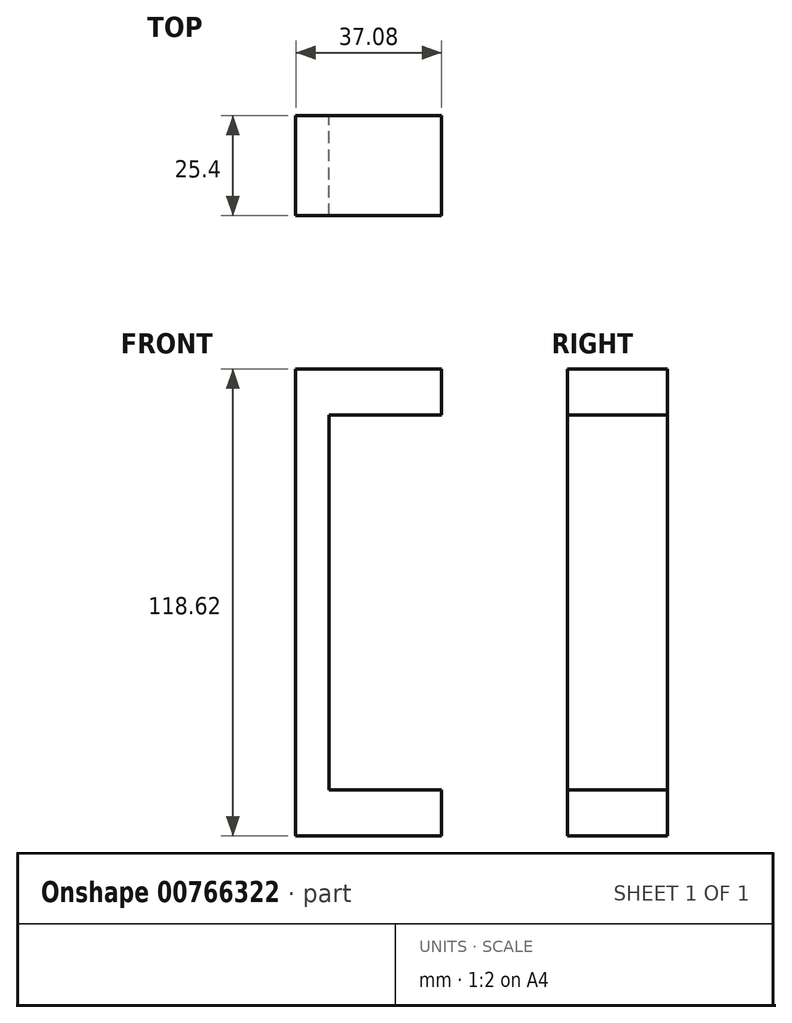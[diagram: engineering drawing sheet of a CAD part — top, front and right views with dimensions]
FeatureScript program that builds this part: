
annotation { "Feature Type Name" : "Feature", "Feature Type Description" : "" }
export const myFeature = defineFeature(function(context is Context, id is Id, definition is map)
    precondition{}
    {
        {
            var Q0;
            Q0=qCreatedBy(makeId("Front.planeOp"),FACE);
            var sketch = newSketch(context, id + "F0", { "sketchPlane" : qUnion([Q0])});
            skLineSegment(sketch, "E0.bottom", {"start": v(28.57, 47.63) * mm, "end": v(-28.58, 47.62) * mm});
            skLineSegment(sketch, "E0.top", {"start": v(28.58, -47.62) * mm, "end": v(-28.57, -47.63) * mm});
            skLineSegment(sketch, "E0.left", {"start": v(28.57, 47.63) * mm, "end": v(28.58, -47.62) * mm});
            skLineSegment(sketch, "E0.right", {"start": v(-28.58, 47.62) * mm, "end": v(-28.57, -47.63) * mm});
            skPoint(sketch, "E0.middle", {"position": v(0, 0) * mm});
            skLineSegment(sketch, "E1.bottom", {"start": v(37.08, 59.3) * mm, "end": v(-37.08, 59.3) * mm});
            skLineSegment(sketch, "E1.top", {"start": v(37.08, -59.3) * mm, "end": v(-37.08, -59.3) * mm});
            skLineSegment(sketch, "E1.left", {"start": v(37.08, 59.3) * mm, "end": v(37.08, -59.3) * mm});
            skLineSegment(sketch, "E1.right", {"start": v(-37.08, 59.3) * mm, "end": v(-37.08, -59.3) * mm});
            skSolve(sketch);
        }
        {
            var Q0;
            Q0=makeQuery(id+"F0.imprint","IMPRINT",FACE,{"disambiguationData":[TD([[makeQuery(id+"F0.imprint","IMPRINT",EDGE,{"derivedFrom":sQuery(id+"F0.wireOp",EDGE,"E0.bottom")}),-1.0]])]});
            extrude(context, id + "F1", {"entities" : qUnion([Q0]), "depth" : 25.4 * mm, "offsetDistance" : 25.4 * mm});
        }
        {
            var Q0;
            Q0=makeQuery(id+"F1.opExtrude","CAP_FACE",FACE,{"disambiguationData":[OSD([sQuery(id+"F0.wireOp",EDGE,"E0.bottom"),sQuery(id+"F0.wireOp",EDGE,"E0.top"),sQuery(id+"F0.wireOp",EDGE,"E0.left"),sQuery(id+"F0.wireOp",EDGE,"E0.right"),sQuery(id+"F0.wireOp",EDGE,"E1.bottom"),sQuery(id+"F0.wireOp",EDGE,"E1.top"),sQuery(id+"F0.wireOp",EDGE,"E1.left"),sQuery(id+"F0.wireOp",EDGE,"E1.right")])],"isStart":false});
            var sketch = newSketch(context, id + "F2", { "sketchPlane" : qUnion([Q0])});
            skLineSegment(sketch, "E2.bottom", {"start": v(37.08, 59.3) * mm, "end": v(0, 59.3) * mm});
            skLineSegment(sketch, "E2.top", {"start": v(37.08, -59.3) * mm, "end": v(0, -59.3) * mm});
            skLineSegment(sketch, "E2.left", {"start": v(37.08, 59.3) * mm, "end": v(37.08, -59.3) * mm});
            skLineSegment(sketch, "E2.right", {"start": v(0, 59.3) * mm, "end": v(0, -59.3) * mm});
            skSolve(sketch);
        }
        {
            var Q0;
            {var subQ5=makeQuery(id+"F1.opExtrude","CAP_EDGE",EDGE,{"disambiguationData":[OSD([sQuery(id+"F0.wireOp",EDGE,"E0.left")])],"isStart":false});Q0=makeQuery(id+"F2.imprint","IMPRINT",FACE,{"disambiguationData":[TD([[makeQuery(id+"F2.imprint","IMPRINT",EDGE,{"derivedFrom":subQ5}),-1.0]])]});}
            var Q1;
            {var subQ1=sQuery(id+"F2.wireOp",EDGE,"E2.bottom");Q1=makeQuery(id+"F2.imprint","IMPRINT",FACE,{"disambiguationData":[TD([[makeQuery(id+"F2.imprint","IMPRINT",EDGE,{"derivedFrom":subQ1}),1.0]])]});}
            extrude(context, id + "F3", {"entities" : qUnion([Q0, Q1]), "operationType" : NewBodyOperationType.REMOVE, "endBound" : BoundingType.THROUGH_ALL, "oppositeDirection" : true, "depth" : 25.4 * mm, "offsetDistance" : 25.4 * mm});
        }
    });
